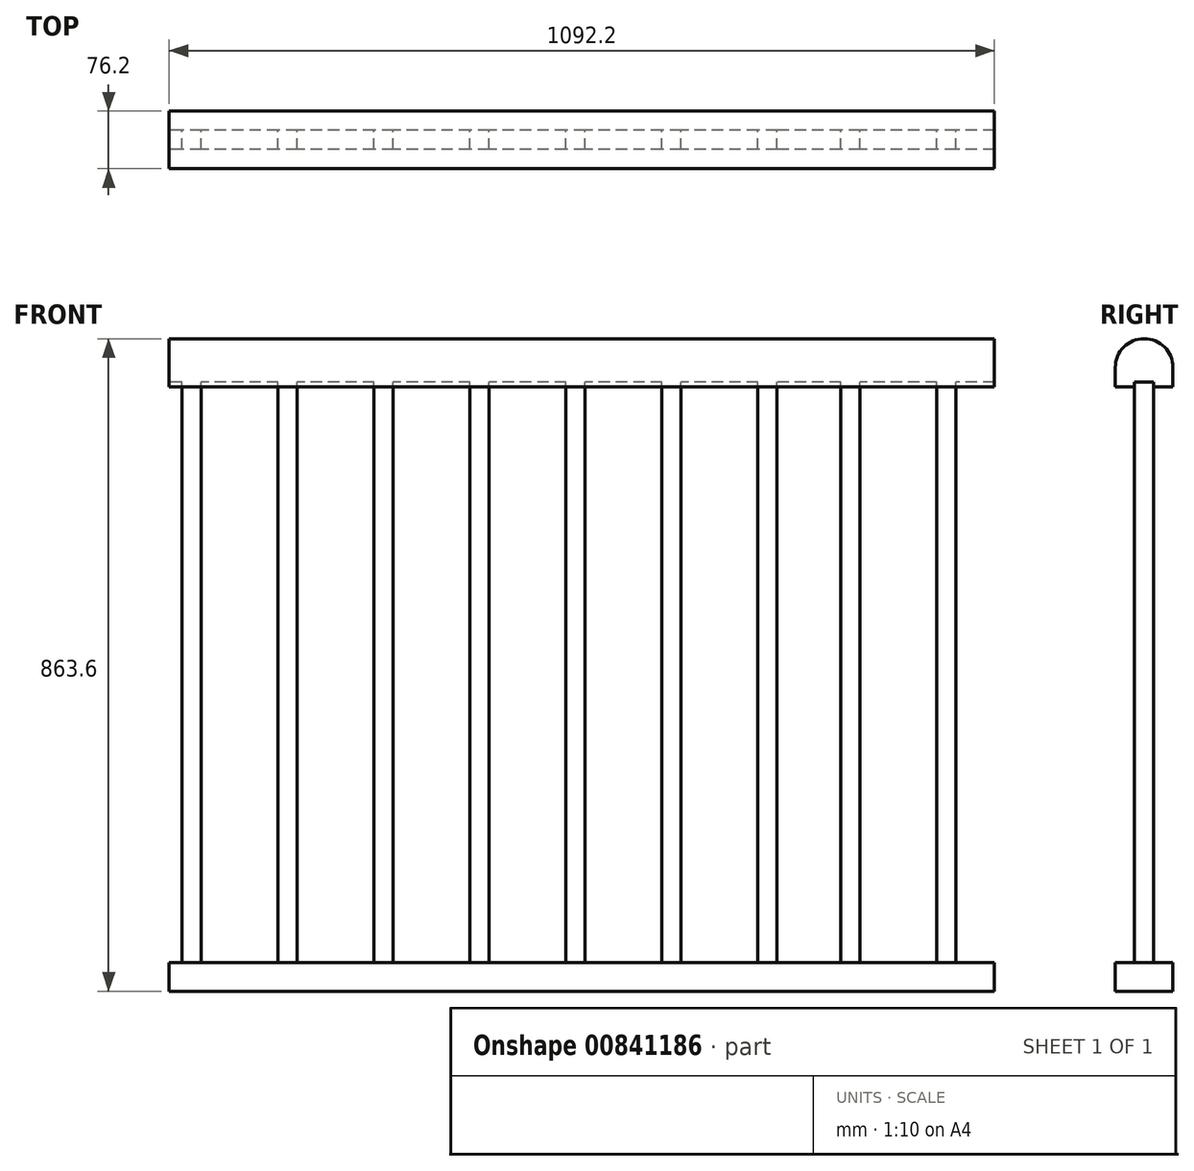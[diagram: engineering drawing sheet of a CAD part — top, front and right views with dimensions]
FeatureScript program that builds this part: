
annotation { "Feature Type Name" : "Feature", "Feature Type Description" : "" }
export const myFeature = defineFeature(function(context is Context, id is Id, definition is map)
    precondition{}
    {
        {
            var Q0;
            Q0=qCreatedBy(makeId("Right.planeOp"),FACE);
            var sketch = newSketch(context, id + "F0", { "sketchPlane" : qUnion([Q0])});
            skLineSegment(sketch, "E0.top", {"start": v(0, -25.4) * mm, "end": v(25.4, -25.4) * mm});
            skLineSegment(sketch, "E0.left", {"start": v(0, 0) * mm, "end": v(0, -25.4) * mm});
            skLineSegment(sketch, "E0.right", {"start": v(76.2, 0) * mm, "end": v(76.2, -25.4) * mm});
            skArc(sketch, "E1", {"start": v(76.2, 0) * mm, "mid": v(38.1, 38.1) * mm, "end": v(0, 0) * mm});
            skLineSegment(sketch, "E2", {"start": v(50.8, -25.4) * mm, "end": v(50.8, -19.05) * mm});
            skLineSegment(sketch, "E3", {"start": v(50.8, -19.05) * mm, "end": v(25.4, -19.05) * mm});
            skLineSegment(sketch, "E4", {"start": v(25.4, -19.05) * mm, "end": v(25.4, -25.4) * mm});
            skLineSegment(sketch, "E5.trimOffspring", {"start": v(50.8, -25.4) * mm, "end": v(76.2, -25.4) * mm});
            skLineSegment(sketch, "E6.bottom", {"start": v(0, -787.4) * mm, "end": v(76.2, -787.4) * mm});
            skLineSegment(sketch, "E6.top", {"start": v(0, -825.5) * mm, "end": v(76.2, -825.5) * mm});
            skLineSegment(sketch, "E6.left", {"start": v(0, -787.4) * mm, "end": v(0, -825.5) * mm});
            skLineSegment(sketch, "E6.right", {"start": v(76.2, -787.4) * mm, "end": v(76.2, -825.5) * mm});
            skSolve(sketch);
        }
        {
            var Q0;
            Q0=makeQuery(id+"F0.imprint","IMPRINT",FACE,{"disambiguationData":[TD([[makeQuery(id+"F0.imprint","IMPRINT",EDGE,{"derivedFrom":sQuery(id+"F0.wireOp",EDGE,"E0.top")}),1.0]])]});
            var Q1;
            Q1=makeQuery(id+"F0.imprint","IMPRINT",FACE,{"disambiguationData":[TD([[makeQuery(id+"F0.imprint","IMPRINT",EDGE,{"derivedFrom":sQuery(id+"F0.wireOp",EDGE,"E6.bottom")}),-1.0]])]});
            extrude(context, id + "F1", {"entities" : qUnion([Q0, Q1]), "depth" : 1092.2 * mm, "offsetDistance" : 25.4 * mm});
        }
        {
            var Q0;
            Q0=makeQuery(id+"F1.opExtrude","SWEPT_FACE",FACE,{"disambiguationData":[OSD([sQuery(id+"F0.wireOp",EDGE,"E3")])]});
            var sketch = newSketch(context, id + "F2", { "sketchPlane" : qUnion([Q0])});
            skLineSegment(sketch, "E7.bottom", {"start": v(1041.4, -25.4) * mm, "end": v(1016, -25.4) * mm});
            skLineSegment(sketch, "E7.top", {"start": v(1041.4, -50.8) * mm, "end": v(1016, -50.8) * mm});
            skLineSegment(sketch, "E7.right", {"start": v(1041.4, -25.4) * mm, "end": v(1041.4, -50.8) * mm});
            skLineSegment(sketch, "E8", {"start": v(1016, -25.4) * mm, "end": v(1016, -50.8) * mm});
            skLineSegment(sketch, "E9.bottom", {"start": v(889, -25.4) * mm, "end": v(914.4, -25.4) * mm});
            skLineSegment(sketch, "E9.top", {"start": v(889, -50.8) * mm, "end": v(914.4, -50.8) * mm});
            skLineSegment(sketch, "E9.left", {"start": v(889, -25.4) * mm, "end": v(889, -50.8) * mm});
            skLineSegment(sketch, "E9.right", {"start": v(914.4, -25.4) * mm, "end": v(914.4, -50.8) * mm});
            skLineSegment(sketch, "E10.bottom", {"start": v(779.28, -25.4) * mm, "end": v(804.68, -25.4) * mm});
            skLineSegment(sketch, "E10.top", {"start": v(779.28, -50.8) * mm, "end": v(804.68, -50.8) * mm});
            skLineSegment(sketch, "E10.left", {"start": v(779.28, -25.4) * mm, "end": v(779.28, -50.8) * mm});
            skLineSegment(sketch, "E10.right", {"start": v(804.68, -25.4) * mm, "end": v(804.68, -50.8) * mm});
            skLineSegment(sketch, "E11.bottom", {"start": v(652.28, -25.4) * mm, "end": v(677.68, -25.4) * mm});
            skLineSegment(sketch, "E11.top", {"start": v(652.28, -50.8) * mm, "end": v(677.68, -50.8) * mm});
            skLineSegment(sketch, "E11.left", {"start": v(652.28, -25.4) * mm, "end": v(652.28, -50.8) * mm});
            skLineSegment(sketch, "E11.right", {"start": v(677.68, -25.4) * mm, "end": v(677.68, -50.8) * mm});
            skLineSegment(sketch, "E12.bottom", {"start": v(525.28, -25.4) * mm, "end": v(550.68, -25.4) * mm});
            skLineSegment(sketch, "E12.top", {"start": v(525.28, -50.8) * mm, "end": v(550.68, -50.8) * mm});
            skLineSegment(sketch, "E12.left", {"start": v(525.28, -25.4) * mm, "end": v(525.28, -50.8) * mm});
            skLineSegment(sketch, "E12.right", {"start": v(550.68, -25.4) * mm, "end": v(550.68, -50.8) * mm});
            skLineSegment(sketch, "E13.bottom", {"start": v(271.28, -25.4) * mm, "end": v(296.68, -25.4) * mm});
            skLineSegment(sketch, "E13.top", {"start": v(271.28, -50.8) * mm, "end": v(296.68, -50.8) * mm});
            skLineSegment(sketch, "E13.left", {"start": v(271.28, -25.4) * mm, "end": v(271.28, -50.8) * mm});
            skLineSegment(sketch, "E13.right", {"start": v(296.68, -25.4) * mm, "end": v(296.68, -50.8) * mm});
            skLineSegment(sketch, "E14.bottom", {"start": v(398.28, -25.4) * mm, "end": v(423.68, -25.4) * mm});
            skLineSegment(sketch, "E14.top", {"start": v(398.28, -50.8) * mm, "end": v(423.68, -50.8) * mm});
            skLineSegment(sketch, "E14.left", {"start": v(398.28, -25.4) * mm, "end": v(398.28, -50.8) * mm});
            skLineSegment(sketch, "E14.right", {"start": v(423.68, -25.4) * mm, "end": v(423.68, -50.8) * mm});
            skLineSegment(sketch, "E15.bottom", {"start": v(144.28, -25.4) * mm, "end": v(169.68, -25.4) * mm});
            skLineSegment(sketch, "E15.top", {"start": v(144.28, -50.8) * mm, "end": v(169.68, -50.8) * mm});
            skLineSegment(sketch, "E15.left", {"start": v(144.28, -25.4) * mm, "end": v(144.28, -50.8) * mm});
            skLineSegment(sketch, "E15.right", {"start": v(169.68, -25.4) * mm, "end": v(169.68, -50.8) * mm});
            skLineSegment(sketch, "E16.bottom", {"start": v(17.28, -25.4) * mm, "end": v(42.68, -25.4) * mm});
            skLineSegment(sketch, "E16.top", {"start": v(17.28, -50.8) * mm, "end": v(42.68, -50.8) * mm});
            skLineSegment(sketch, "E16.left", {"start": v(17.28, -25.4) * mm, "end": v(17.28, -50.8) * mm});
            skLineSegment(sketch, "E16.right", {"start": v(42.68, -25.4) * mm, "end": v(42.68, -50.8) * mm});
            skSolve(sketch);
        }
        {
            var Q0;
            Q0=qSketchRegion(id+"F2",true);
            var Q1;
            Q1=makeQuery(id+"F1.opExtrude","SWEPT_FACE",FACE,{"disambiguationData":[OSD([sQuery(id+"F0.wireOp",EDGE,"E6.bottom")])]});
            extrude(context, id + "F3", {"entities" : qUnion([Q0, Q1]), "operationType" : NewBodyOperationType.ADD, "endBound" : BoundingType.UP_TO_NEXT, "depth" : 25.4 * mm, "offsetDistance" : 25.4 * mm});
        }
    });
